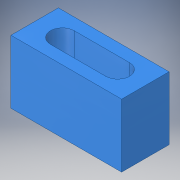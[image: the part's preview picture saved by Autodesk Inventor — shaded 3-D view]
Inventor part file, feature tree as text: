
AUTODESK INVENTOR PART (.ipt)
format: ipt  version: 2018 (Build 220112000, 112)  size: 138,240 bytes
history: native  units: in
note: dims shown in document units (in); Inventor stores cm internally (conversion verified against a paired STEP export)
features: extrude x4, sketch x3, projected_geometry x2
ambient origin geometry x8: Origin, YZ Plane, XZ Plane, XY Plane, X Axis, Y Axis, Z Axis, Center Point
bodies: Body1 (feature_tree)
feature tree (9):
  extrude  "Extrusion5"  Depth=3.5in
  sketch  "Sketch10"  dims[d20=0.3125in d21=1.0in]
  extrude  "Extrusion8"  Depth=1.0in
  extrude  "Extrusion9"  Depth=0.875in
  extrude  "Extrusion10"  Depth=2.0in TaperAngle=0.0deg
  sketch  "Sketch1"  dims[d3=1.5in d4=3.5in]
  projected_geometry  "Projected Loop7"
  sketch  "Sketch12"  dims[d22=0.875in d23=0.875in d24=2.0in d25=0.0in d38=0.38in d39=1.5in d40=0.0in d41=0.75in d42=1.0in d43=0.0in d44=0.5in d45=0.0in]
  projected_geometry  "Projected Loop8"
